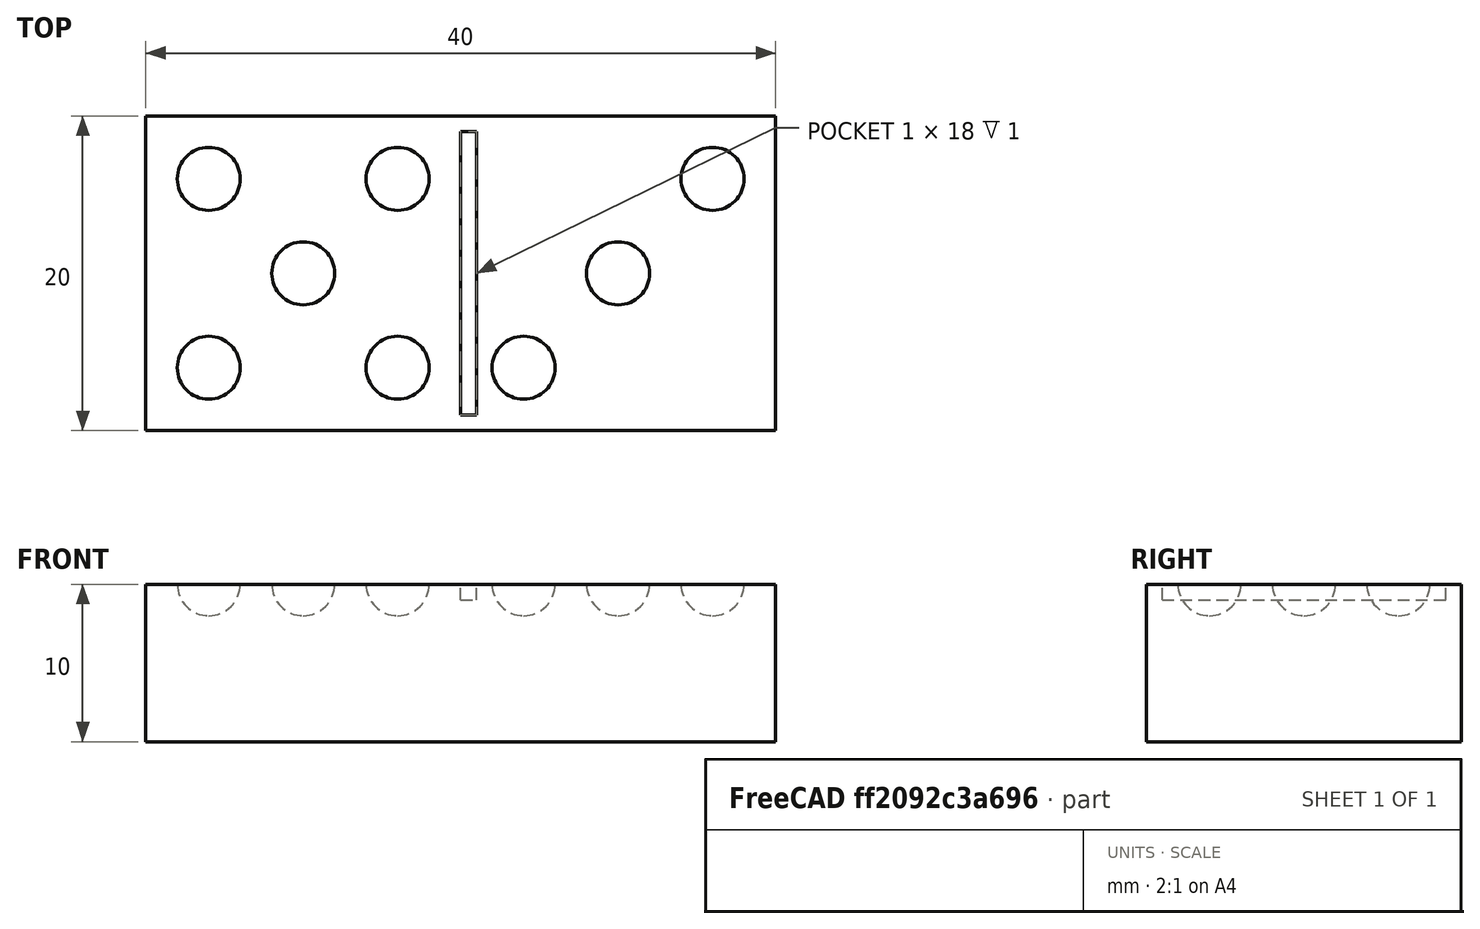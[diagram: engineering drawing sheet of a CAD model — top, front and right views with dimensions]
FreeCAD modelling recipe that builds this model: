
FCSTD DOCUMENT  (FreeCAD 1.0R39319 (Git))
Label: ojt1_t13r03_domino
License: All rights reserved
LicenseURL: https://en.wikipedia.org/wiki/All_rights_reserved
objects: Part::Sphere×9, Part::MultiFuse×3, Part::Box×2, Part::Cut×2
note: 16 computed .brp shape members not serialized (recipe doc carries the construction recipe); baked Part::Feature solids carry a one-line shape summary decoded from their .brp

FEATURE [Part::Box] Box  label="Cube"
  AttacherType = Attacher::AttachEngine3D
  Height = 10
  Length = 40
  Width = 20
FEATURE [Part::Box] Box001  label="Cube001"
  AttacherType = Attacher::AttachEngine3D
  Height = 1
  Length = 1
  Placement = pos=(20,1,9) rot=(0,0,1;0rad)
  Width = 18
FEATURE [Part::Cut] Cut
  Base = -> Box
  Refine = true
  Tool = -> Box001
FEATURE [Part::Sphere] Sphere
  Angle1 = -90
  Angle2 = 90
  Angle3 = 360
  AttacherType = Attacher::AttachEngine3D
  Placement = pos=(4,4,10) rot=(0,0,1;0rad)
  Radius = 2
FEATURE [Part::Sphere] Sphere001
  Angle1 = -90
  Angle2 = 90
  Angle3 = 360
  AttacherType = Attacher::AttachEngine3D
  Placement = pos=(4,16,10) rot=(0,0,1;0rad)
  Radius = 2
FEATURE [Part::MultiFuse] Fusion
  Refine = true
  Shapes = -> [Sphere001,Sphere]
FEATURE [Part::Sphere] Sphere002
  Angle1 = -90
  Angle2 = 90
  Angle3 = 360
  AttacherType = Attacher::AttachEngine3D
  Placement = pos=(4,4,10) rot=(0,0,1;0rad)
  Radius = 2
FEATURE [Part::Sphere] Sphere003
  Angle1 = -90
  Angle2 = 90
  Angle3 = 360
  AttacherType = Attacher::AttachEngine3D
  Placement = pos=(4,16,10) rot=(0,0,1;0rad)
  Radius = 2
FEATURE [Part::MultiFuse] Fusion001
  Placement = pos=(12,0,0) rot=(0,0,1;0rad)
  Refine = true
  Shapes = -> [Sphere003,Sphere002]
FEATURE [Part::Sphere] Sphere004
  Angle1 = -90
  Angle2 = 90
  Angle3 = 360
  AttacherType = Attacher::AttachEngine3D
  Placement = pos=(10,10,10) rot=(0,0,1;0rad)
  Radius = 2
FEATURE [Part::Sphere] Sphere005
  Angle1 = -90
  Angle2 = 90
  Angle3 = 360
  AttacherType = Attacher::AttachEngine3D
  Placement = pos=(24,4,10) rot=(0,0,1;0rad)
  Radius = 2
FEATURE [Part::Sphere] Sphere007
  Angle1 = -90
  Angle2 = 90
  Angle3 = 360
  AttacherType = Attacher::AttachEngine3D
  Placement = pos=(4,16,10) rot=(0,0,1;0rad)
  Radius = 2
FEATURE [Part::Sphere] Sphere008
  Angle1 = -90
  Angle2 = 90
  Angle3 = 360
  AttacherType = Attacher::AttachEngine3D
  Placement = pos=(36,16,10) rot=(0,0,1;0rad)
  Radius = 2
FEATURE [Part::Sphere] Sphere009
  Angle1 = -90
  Angle2 = 90
  Angle3 = 360
  AttacherType = Attacher::AttachEngine3D
  Placement = pos=(30,10,10) rot=(0,0,1;0rad)
  Radius = 2
FEATURE [Part::MultiFuse] Fusion002
  Refine = true
  Shapes = -> [Fusion,Fusion001,Sphere004,Sphere005,Sphere007,Sphere008,Sphere009]
FEATURE [Part::Cut] Cut001
  Base = -> Cut
  Refine = true
  Tool = -> Fusion002
